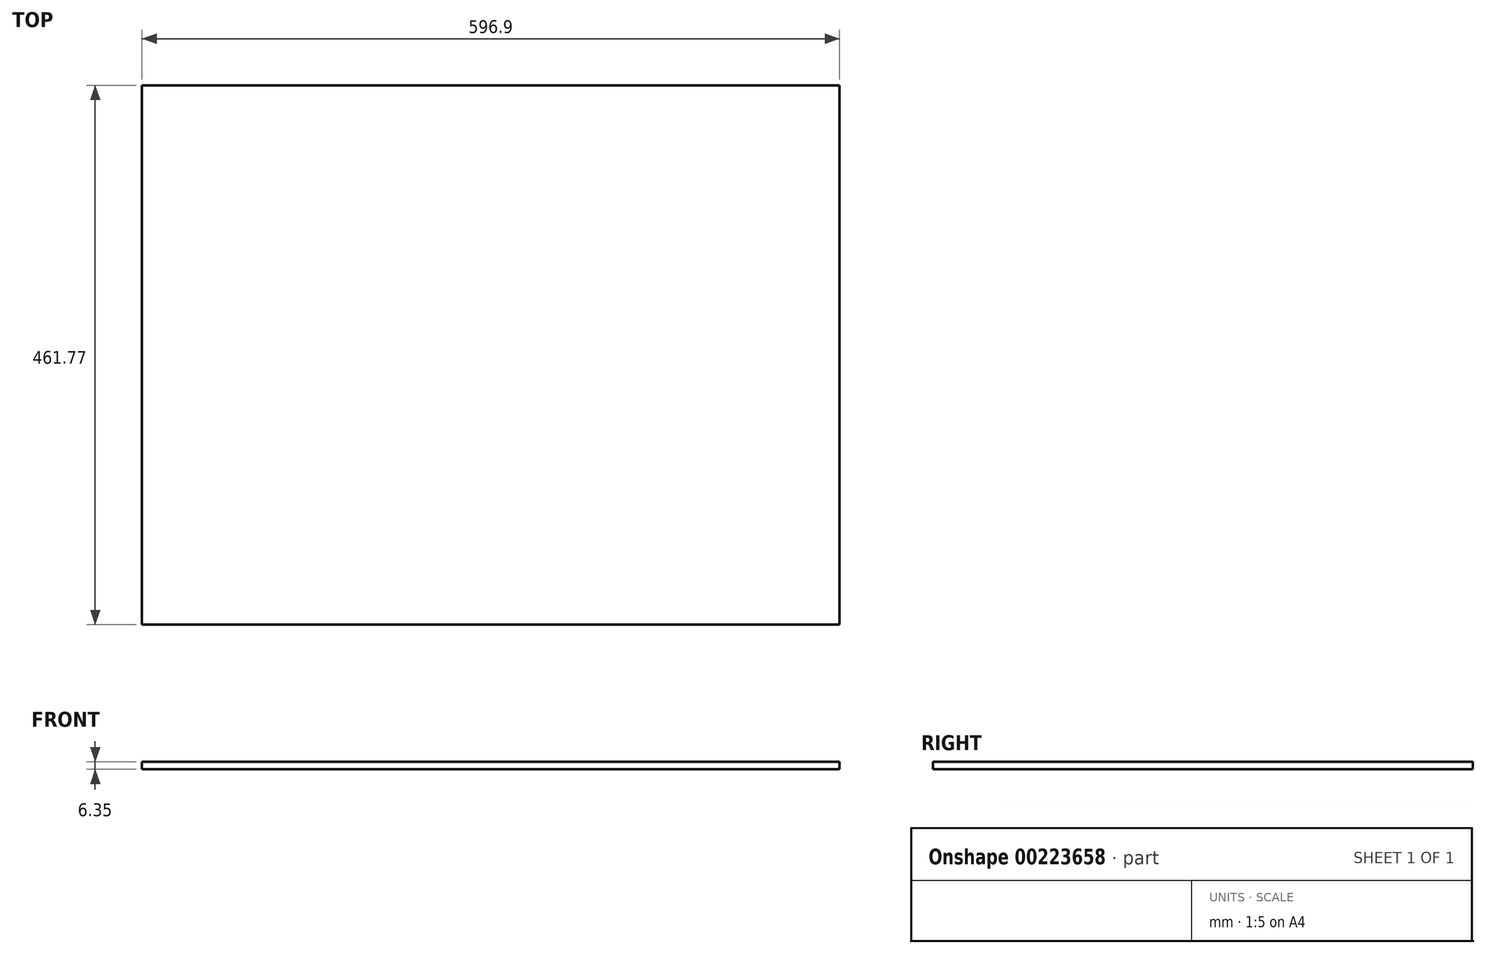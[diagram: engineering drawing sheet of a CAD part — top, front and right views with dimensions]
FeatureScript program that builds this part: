
annotation { "Feature Type Name" : "Feature", "Feature Type Description" : "" }
export const myFeature = defineFeature(function(context is Context, id is Id, definition is map)
    precondition{}
    {
        {
            var Q0;
            Q0=qCreatedBy(makeId("Top.planeOp"),FACE);
            var sketch = newSketch(context, id + "F0", { "sketchPlane" : qUnion([Q0])});
            skLineSegment(sketch, "E0.bottom", {"start": v(-609.8, -234.3) * mm, "end": v(-12.9, -234.3) * mm});
            skLineSegment(sketch, "E0.top", {"start": v(-609.8, 227.47) * mm, "end": v(-12.9, 227.47) * mm});
            skLineSegment(sketch, "E0.left", {"start": v(-609.8, -234.3) * mm, "end": v(-609.8, 227.47) * mm});
            skLineSegment(sketch, "E0.right", {"start": v(-12.9, -234.3) * mm, "end": v(-12.9, 227.47) * mm});
            skSolve(sketch);
        }
        {
            var Q0;
            Q0 = qSketchRegion(id + "F0", true);
            extrude(context, id + "F1", {"entities" : qUnion([Q0]), "oppositeDirection" : true, "depth" : 6.35 * mm});
        }
    });
